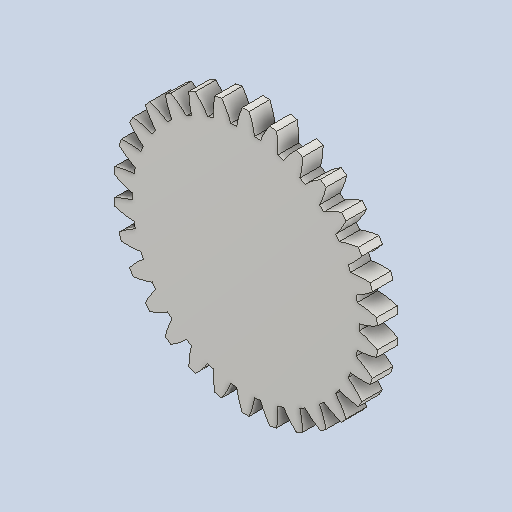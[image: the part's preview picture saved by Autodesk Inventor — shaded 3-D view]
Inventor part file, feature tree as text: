
AUTODESK INVENTOR PART (.ipt)
format: ipt  version: 2024 (Build 280153000, 153)  size: 258,560 bytes
history: native  units: mm (DEFAULTED — no unit token found)
features: plane x3, other x3, extrude x1, sketch x1
ambient origin geometry x8: Origin, YZ Plane, XZ Plane, XY Plane, X Axis, Y Axis, Z Axis, Center Point
bodies: Solid1 (feature_tree)
feature tree (8):
  extrude  "Extrusion1"  Depth=5.0mm TaperAngle=0.0deg
  plane  "Work Plane2"
  plane  "Work Plane8"
  plane  "Work Plane9"
  other  "Spur Gear"
  sketch  "Sketch1"  dims[d0=64.0mm d1=5.0mm d2=0.0mm d3=60.0mm d4=10.0mm d5=0.0mm d16=120.0mm d17=0.0mm d34=1.047198mm d39=0.0mm d41=0.0mm d43=120.0mm d46=120.0mm d47=0.0mm d48=0.0mm]
  other  "Srf1"
  other  "Pitch Diameter"
